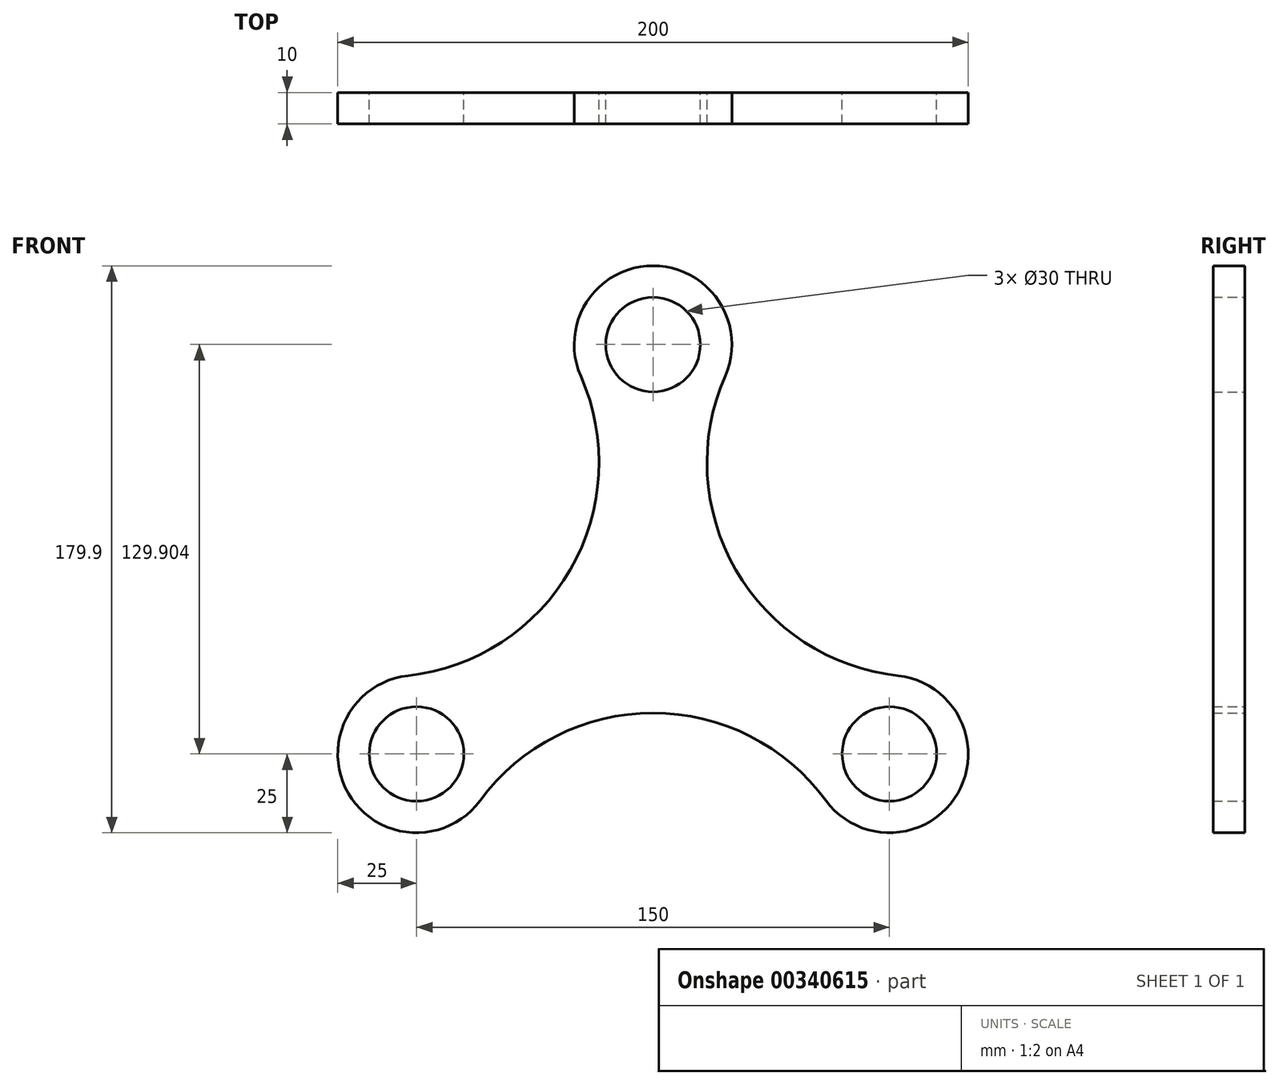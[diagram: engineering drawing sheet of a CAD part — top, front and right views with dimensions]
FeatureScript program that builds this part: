
annotation { "Feature Type Name" : "Feature", "Feature Type Description" : "" }
export const myFeature = defineFeature(function(context is Context, id is Id, definition is map)
    precondition{}
    {
        {
            var Q0;
            Q0=qCreatedBy(makeId("Front.planeOp"),FACE);
            var sketch = newSketch(context, id + "F0", { "sketchPlane" : qUnion([Q0])});
            skCircle(sketch, "E0", {"center": v(0, 129.9) * mm, "radius": 15 * mm});
            skCircle(sketch, "E1", {"center": v(0, 129.9) * mm, "radius": 25 * mm});
            skCircle(sketch, "E2", {"center": v(-75, 0) * mm, "radius": 15 * mm});
            skCircle(sketch, "E3", {"center": v(-75, 0) * mm, "radius": 25 * mm});
            skCircle(sketch, "E4", {"center": v(75, 0) * mm, "radius": 15 * mm});
            skCircle(sketch, "E5", {"center": v(75, 0) * mm, "radius": 25 * mm});
            skLineSegment(sketch, "E6", {"start": v(0, 129.9) * mm, "end": v(-75, 0) * mm, "construction": true});
            skLineSegment(sketch, "E7", {"start": v(75, 0) * mm, "end": v(-75, 0) * mm, "construction": true});
            skLineSegment(sketch, "E8", {"start": v(0, 129.9) * mm, "end": v(75, 0) * mm, "construction": true});
            skPoint(sketch, "E9", {"position": v(-37.5, 64.95) * mm});
            skPoint(sketch, "E10", {"position": v(37.5, 64.95) * mm});
            skPoint(sketch, "E11", {"position": v(0, 0) * mm});
            skPoint(sketch, "E12", {"position": v(-85.12, 92.45) * mm});
            skPoint(sketch, "E13", {"position": v(85.12, 92.45) * mm});
            skPoint(sketch, "E14", {"position": v(0, -55) * mm});
            skCircle(sketch, "E15", {"center": v(-85.12, 92.45) * mm, "radius": 68 * mm, "construction": true});
            skCircle(sketch, "E16", {"center": v(85.12, 92.45) * mm, "radius": 68 * mm, "construction": true});
            skCircle(sketch, "E17", {"center": v(0, -55) * mm, "radius": 68 * mm, "construction": true});
            skArc(sketch, "E18", {"start": v(-77.72, 24.85) * mm, "mid": v(-26.23, 58.45) * mm, "end": v(-22.88, 119.83) * mm, "construction": true});
            skArc(sketch, "E19", {"start": v(-77.72, 24.85) * mm, "mid": v(-26.23, 58.45) * mm, "end": v(-22.88, 119.83) * mm});
            skArc(sketch, "E20", {"start": v(22.88, 119.83) * mm, "mid": v(26.23, 58.45) * mm, "end": v(77.72, 24.85) * mm});
            skArc(sketch, "E21", {"start": v(54.84, -14.78) * mm, "mid": v(0, 13) * mm, "end": v(-54.84, -14.78) * mm});
            skSolve(sketch);
        }
        {
            var Q0;
            Q0 = qSketchRegion(id + "F0", true);
            extrude(context, id + "F1", {"entities" : qUnion([Q0]), "depth" : 5 * mm});
        }
        {
            var Q0;
            Q0 = qSketchRegion(id + "F0", true);
            extrude(context, id + "F2", {"entities" : qUnion([Q0]), "operationType" : NewBodyOperationType.ADD, "depth" : 10 * mm});
        }
    });
